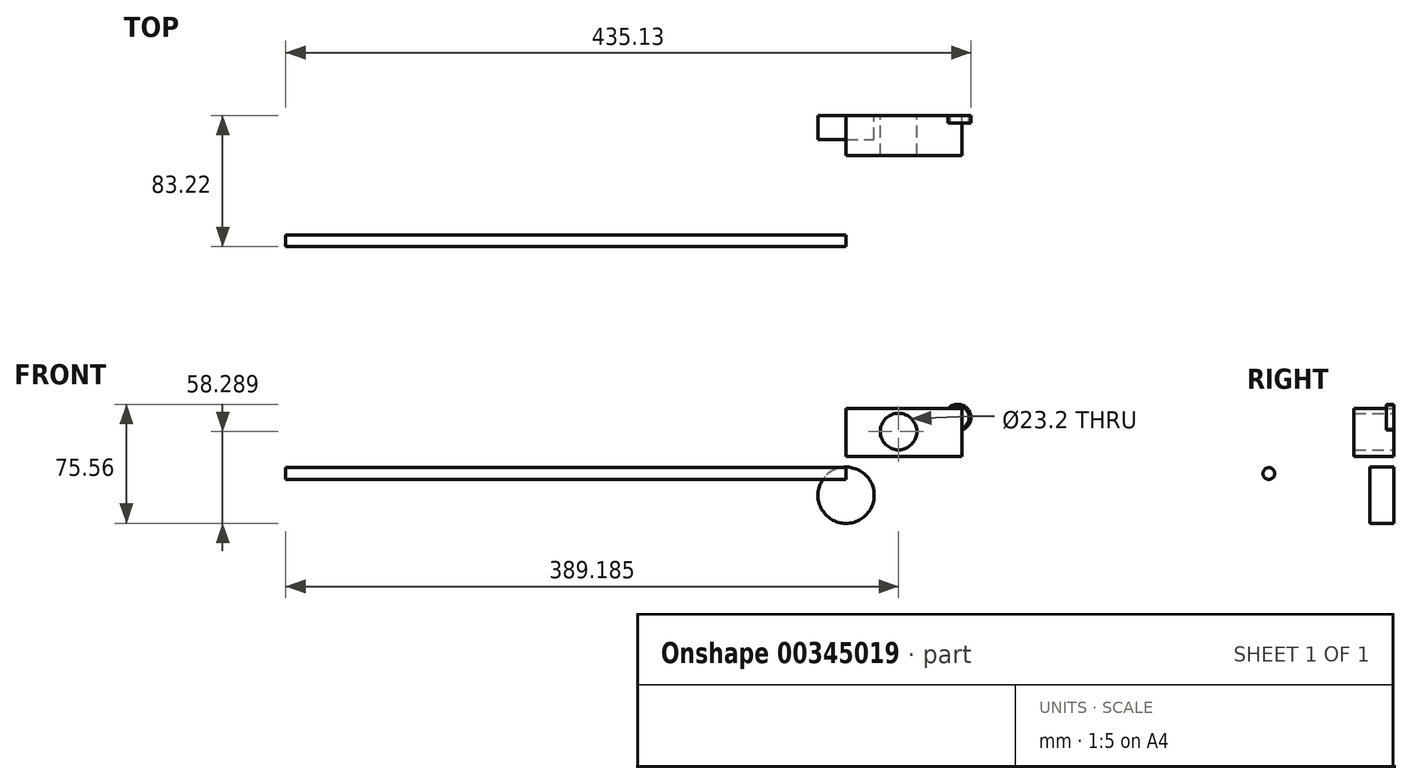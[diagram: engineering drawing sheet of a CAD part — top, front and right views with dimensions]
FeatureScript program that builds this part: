
annotation { "Feature Type Name" : "Feature", "Feature Type Description" : "" }
export const myFeature = defineFeature(function(context is Context, id is Id, definition is map)
    precondition{}
    {
        {
            var Q0;
            Q0=qCreatedBy(makeId("Right.planeOp"),FACE);
            var sketch = newSketch(context, id + "F0", { "sketchPlane" : qUnion([Q0])});
            skCircle(sketch, "E0", {"center": v(-79.48, 13.78) * mm, "radius": 3.74 * mm});
            skSolve(sketch);
        }
        {
            var Q0;
            Q0=makeQuery(id+"F0.imprint","IMPRINT",FACE,{"disambiguationData":[TD([[makeQuery(id+"F0.imprint","IMPRINT",EDGE,{"derivedFrom":sQuery(id+"F0.wireOp",EDGE,"E0")}),1.0]])]});
            extrude(context, id + "F1", {"entities" : qUnion([Q0]), "oppositeDirection" : true, "depth" : 355.85 * mm});
        }
        {
            var Q0;
            Q0=qCreatedBy(makeId("Front.planeOp"),FACE);
            var sketch = newSketch(context, id + "F2", { "sketchPlane" : qUnion([Q0])});
            skCircle(sketch, "E1", {"center": v(70.95, 49.37) * mm, "radius": 7.21 * mm});
            skCircle(sketch, "E2", {"center": v(70.95, 49.37) * mm, "radius": 8.33 * mm});
            skSolve(sketch);
        }
        {
            var Q0;
            Q0 = qSketchRegion(id + "F2", true);
            extrude(context, id + "F3", {"entities" : qUnion([Q0]), "depth" : 4.83 * mm});
        }
        {
            var Q0;
            Q0=qCreatedBy(makeId("Front.planeOp"),FACE);
            var sketch = newSketch(context, id + "F4", { "sketchPlane" : qUnion([Q0])});
            skLineSegment(sketch, "E3.bottom", {"start": v(73.73, 54.94) * mm, "end": v(0, 54.94) * mm});
            skLineSegment(sketch, "E3.top", {"start": v(73.73, 24.5) * mm, "end": v(0, 24.5) * mm});
            skLineSegment(sketch, "E3.left", {"start": v(73.73, 54.94) * mm, "end": v(73.73, 24.5) * mm});
            skLineSegment(sketch, "E3.right", {"start": v(0, 54.94) * mm, "end": v(0, 24.5) * mm});
            skCircle(sketch, "E4", {"center": v(33.33, 40.42) * mm, "radius": 11.6 * mm});
            skSolve(sketch);
        }
        {
            var Q0;
            Q0 = qSketchRegion(id + "F4", true);
            extrude(context, id + "F5", {"entities" : qUnion([Q0]), "operationType" : NewBodyOperationType.ADD, "depth" : 25.4 * mm});
        }
        {
            var Q0;
            Q0=qCreatedBy(makeId("Front.planeOp"),FACE);
            var sketch = newSketch(context, id + "F6", { "sketchPlane" : qUnion([Q0])});
            skCircle(sketch, "E5", {"center": v(0, 0) * mm, "radius": 17.87 * mm});
            skSolve(sketch);
        }
        {
            var Q0;
            Q0 = qSketchRegion(id + "F6", true);
            extrude(context, id + "F7", {"entities" : qUnion([Q0]), "depth" : 15.24 * mm});
        }
    });
